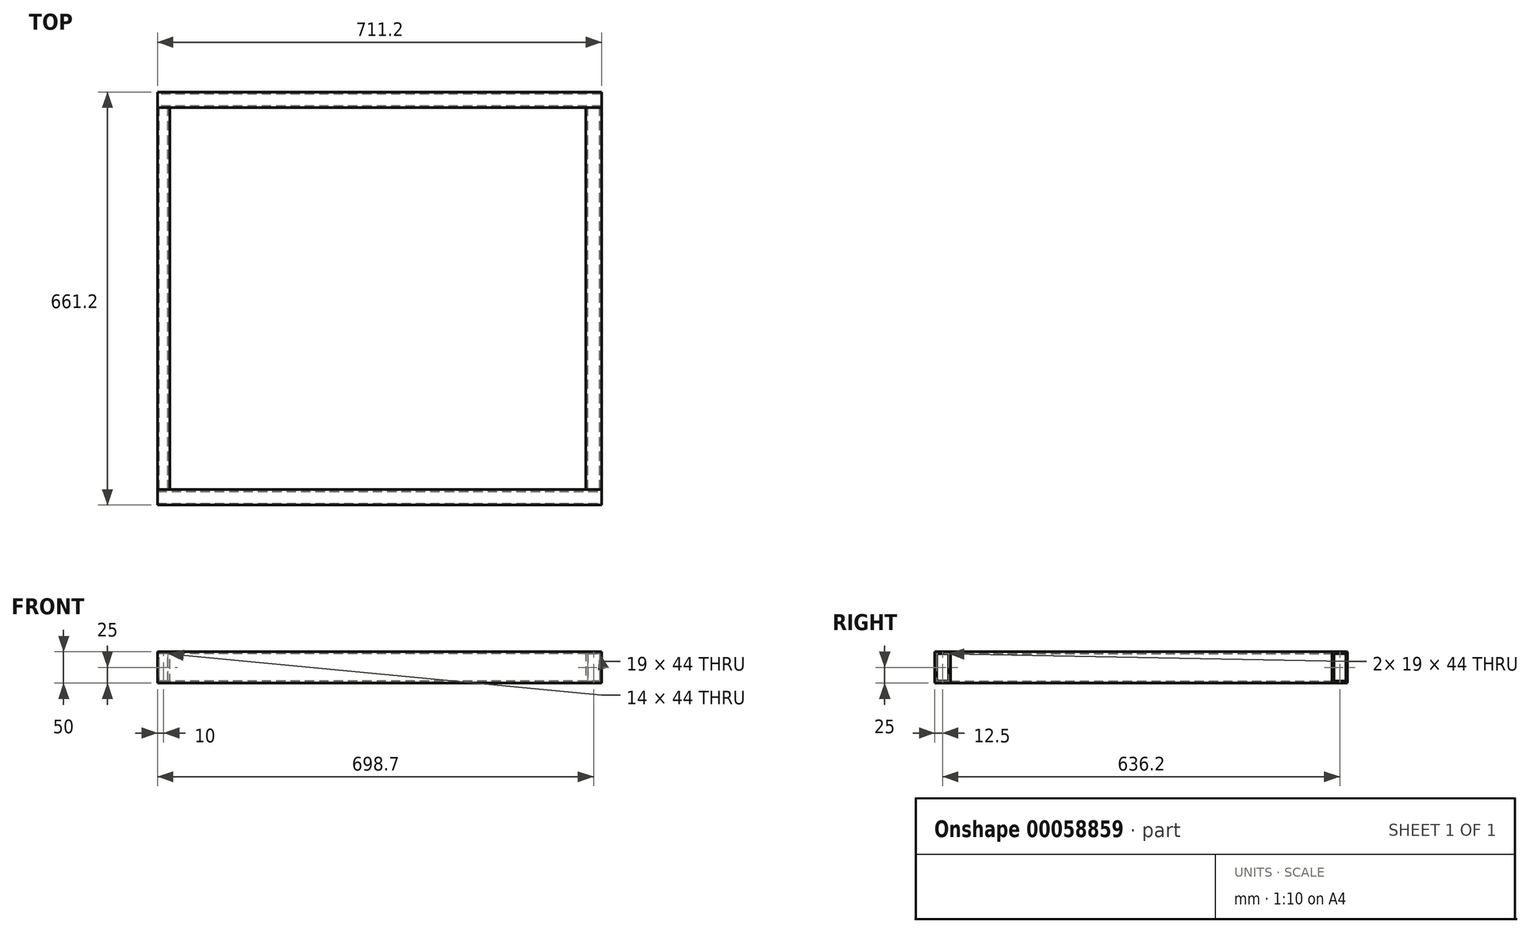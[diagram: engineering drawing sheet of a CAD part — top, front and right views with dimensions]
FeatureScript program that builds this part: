
annotation { "Feature Type Name" : "Feature", "Feature Type Description" : "" }
export const myFeature = defineFeature(function(context is Context, id is Id, definition is map)
    precondition{}
    {
        {
            var Q0;
            Q0=qCreatedBy(makeId("Front.planeOp"),FACE);
            var sketch = newSketch(context, id + "F0", { "sketchPlane" : qUnion([Q0])});
            skLineSegment(sketch, "E0.bottom", {"start": v(0, 0) * mm, "end": v(-20, 0) * mm});
            skLineSegment(sketch, "E0.top", {"start": v(0, 50) * mm, "end": v(-20, 50) * mm});
            skLineSegment(sketch, "E0.left", {"start": v(0, 0) * mm, "end": v(0, 50) * mm});
            skLineSegment(sketch, "E0.right", {"start": v(-20, 0) * mm, "end": v(-20, 50) * mm});
            skLineSegment(sketch, "E1.bottom", {"start": v(-3, 3) * mm, "end": v(-17, 3) * mm});
            skLineSegment(sketch, "E1.top", {"start": v(-3, 47) * mm, "end": v(-17, 47) * mm});
            skLineSegment(sketch, "E1.left", {"start": v(-3, 3) * mm, "end": v(-3, 47) * mm});
            skLineSegment(sketch, "E1.right", {"start": v(-17, 3) * mm, "end": v(-17, 47) * mm});
            skSolve(sketch);
        }
        {
            var Q0;
            Q0=makeQuery(id+"F0.imprint","IMPRINT",FACE,{"disambiguationData":[TD([[makeQuery(id+"F0.imprint","IMPRINT",EDGE,{"derivedFrom":sQuery(id+"F0.wireOp",EDGE,"E0.bottom")}),-1.0]])]});
            extrude(context, id + "F1", {"entities" : qUnion([Q0]), "depth" : 611.2 * mm});
        }
        {
            var Q0;
            Q0=makeQuery(id+"F1.opExtrude","SWEPT_BODY",BODY,{"disambiguationData":[OSD([sQuery(id+"F0.wireOp",EDGE,"E0.bottom"),sQuery(id+"F0.wireOp",EDGE,"E0.top"),sQuery(id+"F0.wireOp",EDGE,"E0.left"),sQuery(id+"F0.wireOp",EDGE,"E0.right"),sQuery(id+"F0.wireOp",EDGE,"E1.bottom"),sQuery(id+"F0.wireOp",EDGE,"E1.top"),sQuery(id+"F0.wireOp",EDGE,"E1.left"),sQuery(id+"F0.wireOp",EDGE,"E1.right")])]});
            transform(context, id + "F2", {"entities" : qUnion([Q0]), "transformType" : TransformType.TRANSLATION_3D, "dx" : 0 * mm, "dy" : 0 * mm, "dz" : 0 * mm, "makeCopy" : true});
        }
        {
            var Q0;
            Q0=makeQuery(id+"F1.opExtrude","SWEPT_FACE",FACE,{"disambiguationData":[OSD([sQuery(id+"F0.wireOp",EDGE,"E0.right")])]});
            var sketch = newSketch(context, id + "F3", { "sketchPlane" : qUnion([Q0])});
            skLineSegment(sketch, "E2.bottom", {"start": v(0, 0) * mm, "end": v(-25, 0) * mm});
            skLineSegment(sketch, "E2.top", {"start": v(0, 50) * mm, "end": v(-25, 50) * mm});
            skLineSegment(sketch, "E2.left", {"start": v(0, 0) * mm, "end": v(0, 50) * mm});
            skLineSegment(sketch, "E2.right", {"start": v(-25, 0) * mm, "end": v(-25, 50) * mm});
            skLineSegment(sketch, "E3.bottom", {"start": v(0, 50) * mm, "end": v(0, 50) * mm});
            skLineSegment(sketch, "E3.top", {"start": v(0, 50) * mm, "end": v(0, 50) * mm});
            skLineSegment(sketch, "E3.left", {"start": v(0, 50) * mm, "end": v(0, 50) * mm});
            skLineSegment(sketch, "E3.right", {"start": v(0, 50) * mm, "end": v(0, 50) * mm});
            skLineSegment(sketch, "E4.0", {"start": v(-3, 3) * mm, "end": v(-22, 3) * mm});
            skLineSegment(sketch, "E4.1", {"start": v(-3, 3) * mm, "end": v(-3, 47) * mm});
            skLineSegment(sketch, "E4.2", {"start": v(-3, 47) * mm, "end": v(-22, 47) * mm});
            skLineSegment(sketch, "E4.3", {"start": v(-22, 3) * mm, "end": v(-22, 47) * mm});
            skSolve(sketch);
        }
        {
            var Q0;
            Q0=makeQuery(id+"F3.imprint","IMPRINT",FACE,{"disambiguationData":[TD([[makeQuery(id+"F3.imprint","IMPRINT",EDGE,{"derivedFrom":sQuery(id+"F3.wireOp",EDGE,"E2.bottom")}),-1.0]])]});
            extrude(context, id + "F4", {"entities" : qUnion([Q0]), "oppositeDirection" : true, "depth" : 711.2 * mm});
        }
        {
            var Q0;
            Q0=makeQuery(id+"F4.opExtrude","SWEPT_FACE",FACE,{"disambiguationData":[OSD([sQuery(id+"F3.wireOp",EDGE,"E2.left")])]});
            var sketch = newSketch(context, id + "F5", { "sketchPlane" : qUnion([Q0])});
            skLineSegment(sketch, "E5.bottom", {"start": v(691.2, 50) * mm, "end": v(666.2, 50) * mm});
            skLineSegment(sketch, "E5.top", {"start": v(691.2, 0) * mm, "end": v(666.2, 0) * mm});
            skLineSegment(sketch, "E5.left", {"start": v(691.2, 50) * mm, "end": v(691.2, 0) * mm});
            skLineSegment(sketch, "E5.right", {"start": v(666.2, 50) * mm, "end": v(666.2, 0) * mm});
            skLineSegment(sketch, "E6.bottom", {"start": v(669.2, 47) * mm, "end": v(688.2, 47) * mm});
            skLineSegment(sketch, "E6.top", {"start": v(669.2, 3) * mm, "end": v(688.2, 3) * mm});
            skLineSegment(sketch, "E6.left", {"start": v(669.2, 47) * mm, "end": v(669.2, 3) * mm});
            skLineSegment(sketch, "E6.right", {"start": v(688.2, 47) * mm, "end": v(688.2, 3) * mm});
            skSolve(sketch);
        }
        {
            var Q0;
            Q0=qSketchRegion(id+"F5",true);
            extrude(context, id + "F6", {"entities" : qUnion([Q0]), "depth" : 611.2 * mm});
        }
        {
            var Q0;
            Q0=makeQuery(id+"F6.opExtrude","SWEPT_FACE",FACE,{"disambiguationData":[OSD([sQuery(id+"F5.wireOp",EDGE,"E5.left")])]});
            var sketch = newSketch(context, id + "F7", { "sketchPlane" : qUnion([Q0])});
            skLineSegment(sketch, "E7.bottom", {"start": v(-611.2, 50) * mm, "end": v(-636.2, 50) * mm});
            skLineSegment(sketch, "E7.top", {"start": v(-611.2, 0) * mm, "end": v(-636.2, 0) * mm});
            skLineSegment(sketch, "E7.left", {"start": v(-611.2, 50) * mm, "end": v(-611.2, 0) * mm});
            skLineSegment(sketch, "E7.right", {"start": v(-636.2, 50) * mm, "end": v(-636.2, 0) * mm});
            skLineSegment(sketch, "E8.0", {"start": v(-614.2, 47) * mm, "end": v(-633.2, 47) * mm});
            skLineSegment(sketch, "E8.1", {"start": v(-614.2, 47) * mm, "end": v(-614.2, 3) * mm});
            skLineSegment(sketch, "E8.2", {"start": v(-614.2, 3) * mm, "end": v(-633.2, 3) * mm});
            skLineSegment(sketch, "E8.3", {"start": v(-633.2, 47) * mm, "end": v(-633.2, 3) * mm});
            skSolve(sketch);
        }
        {
            var Q0;
            Q0=makeQuery(id+"F7.imprint","IMPRINT",FACE,{"disambiguationData":[TD([[makeQuery(id+"F7.imprint","IMPRINT",EDGE,{"derivedFrom":sQuery(id+"F7.wireOp",EDGE,"E7.bottom")}),1.0]])]});
            extrude(context, id + "F8", {"entities" : qUnion([Q0]), "oppositeDirection" : true, "depth" : 711.2 * mm});
        }
        {
            var Q0;
            Q0=makeQuery(id+"F2.opPattern","COPY",BODY,{"derivedFrom":makeQuery(id+"F1.opExtrude","SWEPT_BODY",BODY,{"disambiguationData":[OSD([sQuery(id+"F0.wireOp",EDGE,"E0.bottom"),sQuery(id+"F0.wireOp",EDGE,"E0.top"),sQuery(id+"F0.wireOp",EDGE,"E0.left"),sQuery(id+"F0.wireOp",EDGE,"E0.right"),sQuery(id+"F0.wireOp",EDGE,"E1.bottom"),sQuery(id+"F0.wireOp",EDGE,"E1.top"),sQuery(id+"F0.wireOp",EDGE,"E1.left"),sQuery(id+"F0.wireOp",EDGE,"E1.right")])]}),"instanceName":"1"});
            deleteBodies(context, id + "F9", {"entities" : qUnion([Q0])});
        }
    });
